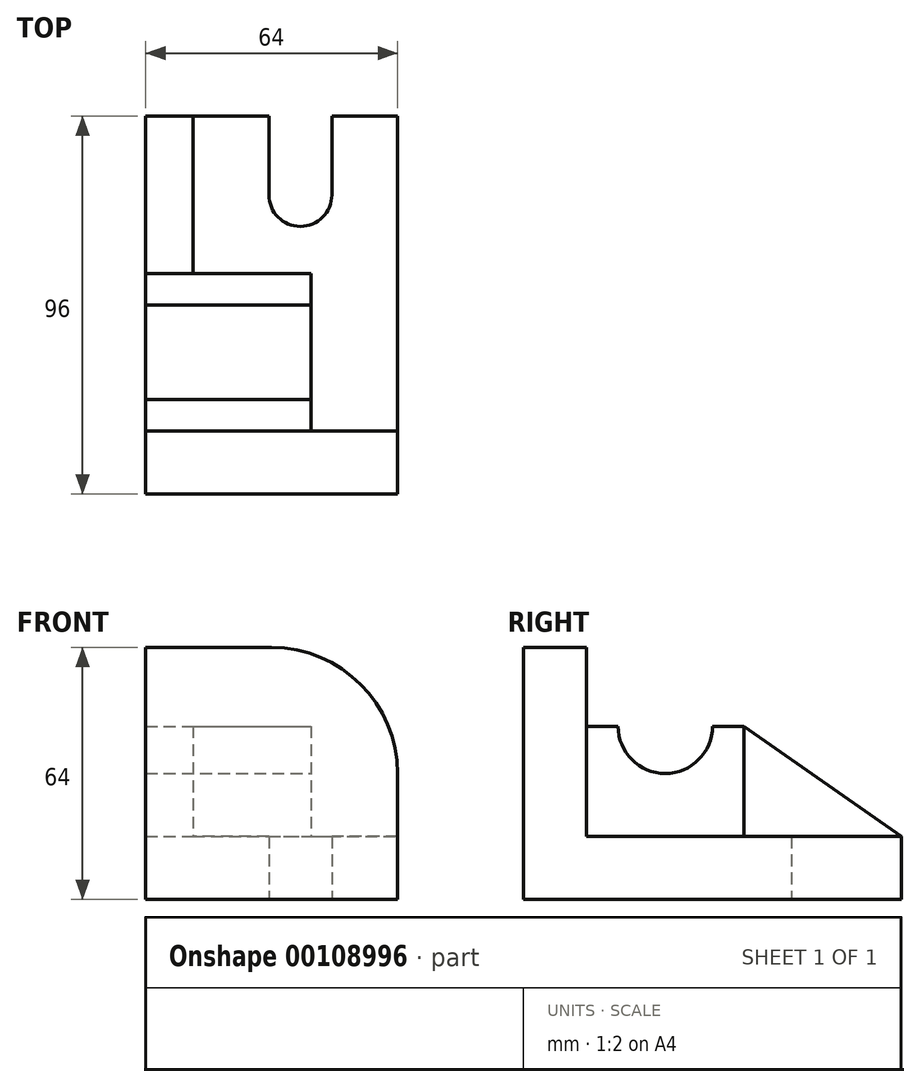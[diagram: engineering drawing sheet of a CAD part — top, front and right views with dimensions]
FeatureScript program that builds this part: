
annotation { "Feature Type Name" : "Feature", "Feature Type Description" : "" }
export const myFeature = defineFeature(function(context is Context, id is Id, definition is map)
    precondition{}
    {
        {
            var Q0;
            Q0=qCreatedBy(makeId("Top.planeOp"),FACE);
            var sketch = newSketch(context, id + "F0", { "sketchPlane" : qUnion([Q0])});
            skLineSegment(sketch, "E0", {"start": v(44.93, -39.27) * mm, "end": v(44.93, 56.73) * mm});
            skLineSegment(sketch, "E1", {"start": v(44.93, 56.73) * mm, "end": v(28.23, 56.73) * mm});
            skLineSegment(sketch, "E2", {"start": v(-19.07, 56.73) * mm, "end": v(-19.07, -39.27) * mm});
            skLineSegment(sketch, "E3", {"start": v(-19.07, -39.27) * mm, "end": v(44.93, -39.27) * mm});
            skLineSegment(sketch, "E4", {"start": v(28.23, 56.73) * mm, "end": v(28.23, 36.73) * mm});
            skLineSegment(sketch, "E5", {"start": v(12.23, 36.73) * mm, "end": v(12.23, 56.73) * mm});
            skArc(sketch, "E6", {"start": v(12.23, 36.73) * mm, "mid": v(20.23, 28.73) * mm, "end": v(28.23, 36.73) * mm});
            skLineSegment(sketch, "E7.trimOffspring", {"start": v(12.23, 56.73) * mm, "end": v(-19.07, 56.73) * mm});
            skSolve(sketch);
        }
        {
            var Q0;
            Q0 = qSketchRegion(id + "F0", true);
            extrude(context, id + "F1", {"entities" : qUnion([Q0]), "depth" : 16 * mm});
        }
        {
            var Q0;
            Q0=makeQuery(id+"F1.opExtrude","CAP_FACE",FACE,{"disambiguationData":[OSD([sQuery(id+"F0.wireOp",EDGE,"E0"),sQuery(id+"F0.wireOp",EDGE,"E1"),sQuery(id+"F0.wireOp",EDGE,"E2"),sQuery(id+"F0.wireOp",EDGE,"E3"),sQuery(id+"F0.wireOp",EDGE,"E4"),sQuery(id+"F0.wireOp",EDGE,"E5"),sQuery(id+"F0.wireOp",EDGE,"E6"),sQuery(id+"F0.wireOp",EDGE,"E7.trimOffspring")])],"isStart":false});
            var sketch = newSketch(context, id + "F2", { "sketchPlane" : qUnion([Q0])});
            skLineSegment(sketch, "E8.bottom", {"start": v(-19.07, -39.27) * mm, "end": v(44.93, -39.27) * mm});
            skLineSegment(sketch, "E8.top", {"start": v(-19.07, -23.27) * mm, "end": v(44.93, -23.27) * mm});
            skLineSegment(sketch, "E8.left", {"start": v(-19.07, -39.27) * mm, "end": v(-19.07, -23.27) * mm});
            skLineSegment(sketch, "E8.right", {"start": v(44.93, -39.27) * mm, "end": v(44.93, -23.27) * mm});
            skSolve(sketch);
        }
        {
            var Q0;
            Q0 = qSketchRegion(id + "F2", true);
            extrude(context, id + "F3", {"entities" : qUnion([Q0]), "operationType" : NewBodyOperationType.ADD, "depth" : 48 * mm});
        }
        {
            var Q0;
            Q0=makeQuery(id+"F3.opExtrude","CAP_EDGE",EDGE,{"disambiguationData":[OSD([sQuery(id+"F2.wireOp",EDGE,"E8.right")])],"isStart":false});
            fillet(context, id + "F4", {"entities" : qUnion([Q0]), "radius" : 32 * mm, "tangentPropagation" : true, "allowEdgeOverflow" : false});
        }
        {
            var Q0;
            Q0=makeQuery(id+"F1.opExtrude","CAP_FACE",FACE,{"disambiguationData":[OSD([sQuery(id+"F0.wireOp",EDGE,"E0"),sQuery(id+"F0.wireOp",EDGE,"E1"),sQuery(id+"F0.wireOp",EDGE,"E2"),sQuery(id+"F0.wireOp",EDGE,"E3"),sQuery(id+"F0.wireOp",EDGE,"E4"),sQuery(id+"F0.wireOp",EDGE,"E5"),sQuery(id+"F0.wireOp",EDGE,"E6"),sQuery(id+"F0.wireOp",EDGE,"E7.trimOffspring")])],"isStart":false});
            var sketch = newSketch(context, id + "F5", { "sketchPlane" : qUnion([Q0])});
            skLineSegment(sketch, "E9.bottom", {"start": v(-19.07, -23.27) * mm, "end": v(22.93, -23.27) * mm});
            skLineSegment(sketch, "E9.top", {"start": v(-19.07, 16.73) * mm, "end": v(22.93, 16.73) * mm});
            skLineSegment(sketch, "E9.left", {"start": v(-19.07, -23.27) * mm, "end": v(-19.07, 16.73) * mm});
            skLineSegment(sketch, "E9.right", {"start": v(22.93, -23.27) * mm, "end": v(22.93, 16.73) * mm});
            skSolve(sketch);
        }
        {
            var Q0;
            Q0 = qSketchRegion(id + "F5", true);
            extrude(context, id + "F6", {"entities" : qUnion([Q0]), "operationType" : NewBodyOperationType.ADD, "depth" : 28 * mm});
        }
        {
            var Q0;
            Q0=makeQuery(id+"F6.opExtrude","SWEPT_FACE",FACE,{"disambiguationData":[OSD([sQuery(id+"F5.wireOp",EDGE,"E9.right")])]});
            var sketch = newSketch(context, id + "F7", { "sketchPlane" : qUnion([Q0])});
            skArc(sketch, "E10", {"start": v(-15.27, 44) * mm, "mid": v(-3.27, 32) * mm, "end": v(8.73, 44) * mm});
            skLineSegment(sketch, "E11", {"start": v(-15.27, 44) * mm, "end": v(8.73, 44) * mm});
            skSolve(sketch);
        }
        {
            var Q0;
            Q0 = qSketchRegion(id + "F7", true);
            extrude(context, id + "F8", {"entities" : qUnion([Q0]), "operationType" : NewBodyOperationType.REMOVE, "oppositeDirection" : true, "depth" : 50 * mm});
        }
        {
            var Q0;
            Q0=makeQuery(id+"F1.opExtrude","CAP_FACE",FACE,{"disambiguationData":[OSD([sQuery(id+"F0.wireOp",EDGE,"E0"),sQuery(id+"F0.wireOp",EDGE,"E1"),sQuery(id+"F0.wireOp",EDGE,"E2"),sQuery(id+"F0.wireOp",EDGE,"E3"),sQuery(id+"F0.wireOp",EDGE,"E4"),sQuery(id+"F0.wireOp",EDGE,"E5"),sQuery(id+"F0.wireOp",EDGE,"E6"),sQuery(id+"F0.wireOp",EDGE,"E7.trimOffspring")])],"isStart":false});
            var sketch = newSketch(context, id + "F9", { "sketchPlane" : qUnion([Q0])});
            skLineSegment(sketch, "E12.bottom", {"start": v(-19.07, 16.73) * mm, "end": v(-7.07, 16.73) * mm});
            skLineSegment(sketch, "E12.top", {"start": v(-19.07, 56.73) * mm, "end": v(-7.07, 56.73) * mm});
            skLineSegment(sketch, "E12.left", {"start": v(-19.07, 16.73) * mm, "end": v(-19.07, 56.73) * mm});
            skLineSegment(sketch, "E12.right", {"start": v(-7.07, 16.73) * mm, "end": v(-7.07, 56.73) * mm});
            skSolve(sketch);
        }
        {
            var Q0;
            Q0 = qSketchRegion(id + "F9", true);
            extrude(context, id + "F10", {"entities" : qUnion([Q0]), "operationType" : NewBodyOperationType.ADD, "depth" : 28 * mm});
        }
        {
            var Q0;
            Q0=makeQuery(id+"F6.opExtrude","CAP_EDGE",EDGE,{"disambiguationData":[OSD([sQuery(id+"F5.wireOp",EDGE,"E9.top")])],"isStart":false});
            var Q1;
            Q1=makeQuery(id+"F1.opExtrude","CAP_EDGE",EDGE,{"disambiguationData":[OSD([sQuery(id+"F0.wireOp",EDGE,"E7.trimOffspring")])],"isStart":false});
            cPlane(context, id + "F11", {"entities" : qUnion([Q0, Q1]), "cplaneType" : CPlaneType.LINE_ANGLE, "offset" : 25 * mm, "angle" : 0 * degree, "width" : 150 * mm, "height" : 150 * mm});
        }
        {
            var Q0;
            Q0=qCreatedBy(id+"F11.planeOp",FACE);
            var sketch = newSketch(context, id + "F12", { "sketchPlane" : qUnion([Q0])});
            skLineSegment(sketch, "E13.bottom", {"start": v(-19.07, -11.53) * mm, "end": v(-7.07, -11.53) * mm});
            skLineSegment(sketch, "E13.top", {"start": v(-19.07, 37.3) * mm, "end": v(-7.07, 37.3) * mm});
            skLineSegment(sketch, "E13.left", {"start": v(-19.07, -11.53) * mm, "end": v(-19.07, 37.3) * mm});
            skLineSegment(sketch, "E13.right", {"start": v(-7.07, -11.53) * mm, "end": v(-7.07, 37.3) * mm});
            skSolve(sketch);
        }
        {
            var Q0;
            Q0 = qSketchRegion(id + "F12", true);
            extrude(context, id + "F13", {"entities" : qUnion([Q0]), "operationType" : NewBodyOperationType.REMOVE, "depth" : 25 * mm});
        }
    });
